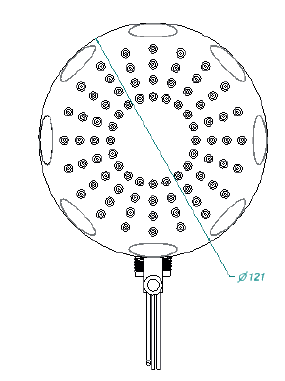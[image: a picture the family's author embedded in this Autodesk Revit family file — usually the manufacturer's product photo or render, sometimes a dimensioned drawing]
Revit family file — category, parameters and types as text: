
# Revit family: 734300001_Ducha Electrica 110V Power 3T
name_source: partatom
category: Plumbing Fixtures
units: mm (PartAtom-declared; Revit-internal decimal feet)

## family parameters
Always vertical = Yes
Cut with Voids When Loaded = No
Host = Wall
OmniClass Number = 23.31.17.00
OmniClass Title = Showers
Part Type = Normal
Room Calculation Point = No
Round Connector Dimension = Use Diameter
Shared = No

## types (1)
- Type 1
    Cableado mínimo = 10 mm2 - 8 AWG
    Corriente Nominal = 36.8 A
    Creado por = BIMBAU
    Default Elevation = 0 mm  [stored 0 ft]
    Description = Ducha eléctrica con certificación RETIE fabricado en aleaciones de cobre, acero, plata, níquel, cromo, aluminio, elastómeros y termoplásticos. 3 temperaturas (FRIO, TÍBIO Y CALIENTE) es posible alcanzar la temperatura ideal y tener el consumo de energía eléctrica de acuerdo a la necesidad. En días y/o regiones más frías, se puede disfrutar de agua caliente en la posición CALIENTE y en días calientes, la economía puede alcanzar 65%, utilizando la ducha en la posición TÍBIA.
    Dimensión de la regadera = 150 x 121 x 121 mm
    Diámetro = 121 mm  [stored 0.396982 ft]
    Fecha de creación = 22/06/2021
    Garantía = 2 años
    Grado de protección = IP24
    Interruptor Requerido = 40 A
    Largo = 150 mm
    Manufacturer = Grival
    Material = Corona_Plastico_Blanco
    Normatividad = NBR 12483, NBR 12087, NBR 12089, NBR 12090
    Peso neto = 390 g. - 0.86 lb
    Potencia Nominal = 4050 W
    Presión máxima recomendada = 58 psi
    Presión mínima recomendada = 14.5 psi
    Productos compatibles = Brazo DH Electrica con malla, Brazo DH Electrica Telescopio
    Referencia = 734300001
    Resistencia = Resistente a la corrosión, pelado y decoloración por agua
    Resistividad mínima del agua = 1300 Ω cm
    Temperatura de uso = Entre 5˚C / 41 ° F a 71˚C / 159,8 °F
    Tensión nominal = 110 V
    URL = https://www.grival.com
    Uso = Residencial

note: [stored X ft] marks values corroborated as IEEE doubles in the binary element streams (Revit-internal decimal feet)

## geometry (parser evidence)
native form markers: Sweep x3
no freeform markers — native parametric forms only
